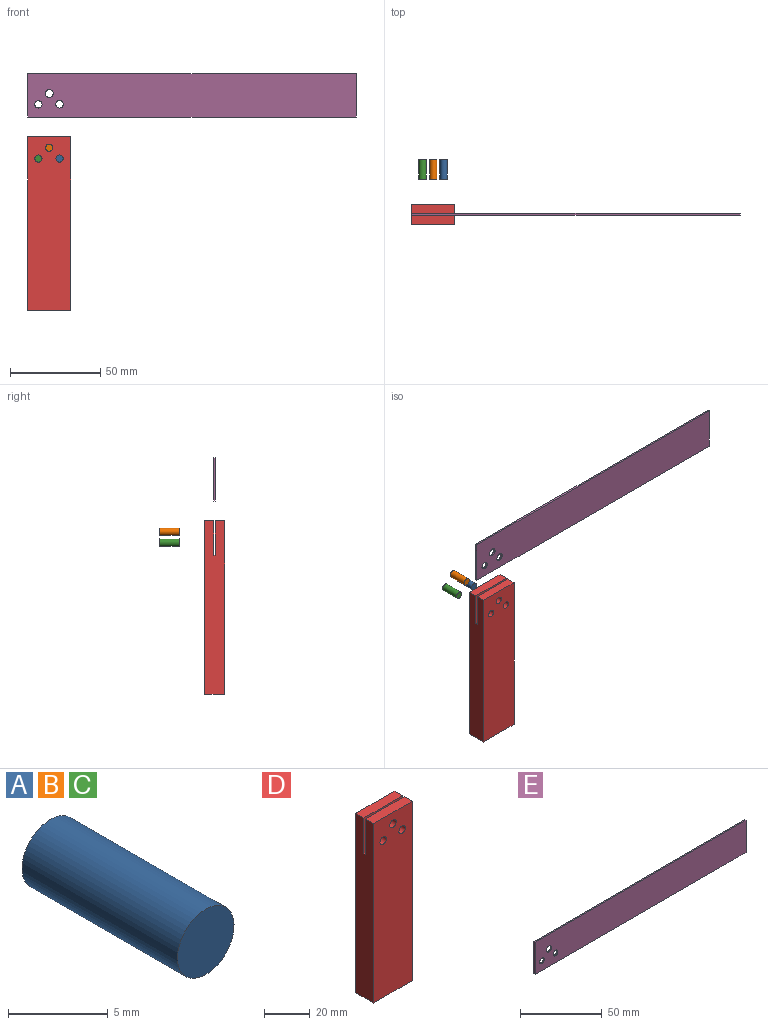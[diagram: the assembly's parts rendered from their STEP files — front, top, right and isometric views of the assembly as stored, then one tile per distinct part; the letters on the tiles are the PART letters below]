
ASSEMBLY  parts=5 mates=4
PART A: 3 faces, bbox 4x11x4 mm
  f0: plane 4x4mm, normal (0,-1,0), area 12.6mm2, adj f1
  f1: cylinder r=2mm len=11mm, axis (0,1,0), area 138.2mm2, adj f0,f2
  f2: plane 4x4mm, normal (0,1,0), area 12.6mm2, adj f1
PART B: same geometry as A
PART C: same geometry as A
PART D: 16 faces, bbox 24x11x96 mm
  f0: plane 24x5mm, normal (0,0,1), area 120mm2, adj f1,f4,f5,f9
  f1: plane 96x11mm, normal (-1,0,0), area 1037mm2, adj f0,f2,f3,f5,f6,f7,f8,f9
  f2: plane 24x5mm, normal (0,0,1), area 120mm2, adj f1,f4,f6,f7
  f3: plane 24x11mm, normal (0,0,-1), area 264mm2, adj f1,f4,f5,f6
  f4: plane 96x11mm, normal (1,0,0), area 1037mm2, adj f0,f2,f3,f5,f6,f7,f8,f9
  f5: plane 96x24mm, normal (0,-1,0), area 2266.3mm2, adj f0,f1,f3,f4,f10,f11,f12
  f6: plane 96x24mm, normal (0,1,0), area 2266.3mm2, adj f1,f2,f3,f4,f13,f14,f15
  f7: plane 24x19mm, normal (0,-1,0), area 418.3mm2, adj f1,f2,f4,f8,f13,f14,f15
  f8: plane 24x1mm, normal (0,0,1), area 24mm2, adj f1,f4,f7,f9
  f9: plane 24x19mm, normal (0,1,0), area 418.3mm2, adj f0,f1,f4,f8,f10,f11,f12
  f10: cylinder r=2mm len=5mm, axis (0,-1,0), area 62.8mm2, adj f5,f9
  f11: cylinder r=2mm len=5mm, axis (0,-1,0), area 62.8mm2, adj f5,f9
  f12: cylinder r=2mm len=5mm, axis (0,-1,0), area 62.8mm2, adj f5,f9
  f13: cylinder r=2mm len=5mm, axis (0,-1,0), area 62.8mm2, adj f6,f7
  f14: cylinder r=2mm len=5mm, axis (0,-1,0), area 62.8mm2, adj f6,f7
  f15: cylinder r=2mm len=5mm, axis (0,-1,0), area 62.8mm2, adj f6,f7
PART E: 9 faces, bbox 182x0.9x24 mm
  f0: plane 24x0.9mm, normal (-1,0,0), area 21.6mm2, adj f1,f3,f4,f5
  f1: plane 182x0.9mm, normal (0,0,-1), area 163.8mm2, adj f0,f2,f4,f5
  f2: plane 24x0.9mm, normal (1,0,0), area 21.6mm2, adj f1,f3,f4,f5
  f3: plane 182x0.9mm, normal (0,0,1), area 163.8mm2, adj f0,f2,f4,f5
  f4: plane 182x24mm, normal (0,-1,0), area 4327.1mm2, adj f0,f1,f2,f3,f6,f7,f8
  f5: plane 182x24mm, normal (0,1,0), area 4327.1mm2, adj f0,f1,f2,f3,f6,f7,f8
  f6: cylinder r=2.05mm len=4.09mm, axis (0,-1,0), area 11.6mm2, adj f4,f5
  f7: cylinder r=2.02mm len=4.04mm, axis (0,-1,0), area 11.4mm2, adj f4,f5
  f8: cylinder r=2.18mm len=4.36mm, axis (0,-1,0), area 12.3mm2, adj f4,f5
PLACE A t=(-25.62,-0.35,-7.77)mm
PLACE B t=(-31.32,-0.35,-1.77)mm
PLACE C t=(-37.32,-0.35,-7.77)mm
PLACE D t=(-31.32,-25.35,-1.77)mm fixed
PLACE E t=(13.24,-30.35,50.74)mm
MATE fastened E.f0 <-> D.f1  axis (-1,0,0) through (-55.91,-30.35,50.74)mm
MATE fastened C.f1 <-> D.f11  axis (0,1,0) through (-49.91,-0.35,27.74)mm
MATE fastened B.f1 <-> D.f12  axis (0,1,0) through (-43.91,-0.35,33.74)mm
MATE fastened A.f1 <-> D.f10  axis (0,1,0) through (-38.21,-0.35,27.74)mm
